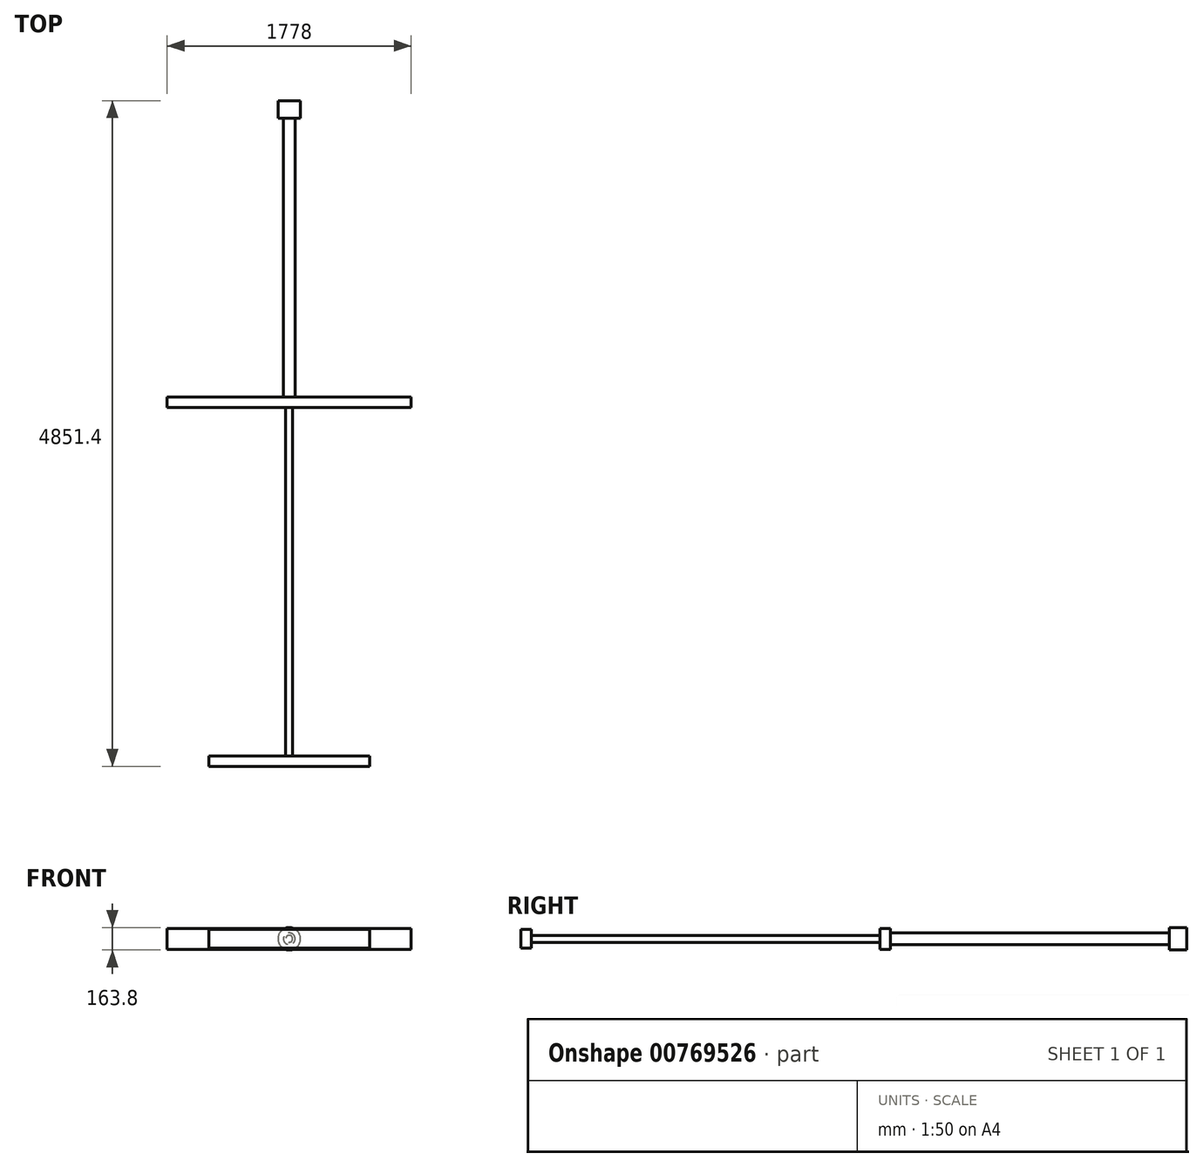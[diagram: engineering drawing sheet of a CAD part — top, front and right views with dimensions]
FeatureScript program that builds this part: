
annotation { "Feature Type Name" : "Feature", "Feature Type Description" : "" }
export const myFeature = defineFeature(function(context is Context, id is Id, definition is map)
    precondition{}
    {
        {
            var Q0;
            Q0=qCreatedBy(makeId("Front.planeOp"),FACE);
            var sketch = newSketch(context, id + "F0", { "sketchPlane" : qUnion([Q0])});
            skCircle(sketch, "E0", {"center": v(0, 0) * mm, "radius": 25.4 * mm});
            skSolve(sketch);
        }
        {
            var Q0;
            Q0 = qSketchRegion(id + "F0", true);
            extrude(context, id + "F1", {"entities" : qUnion([Q0]), "depth" : 2540 * mm, "offsetDistance" : 25.4 * mm});
        }
        {
            var Q0;
            Q0=makeQuery(id+"F1.opExtrude","CAP_FACE",FACE,{"disambiguationData":[OSD([sQuery(id+"F0.wireOp",EDGE,"E0")])],"isStart":false});
            var sketch = newSketch(context, id + "F2", { "sketchPlane" : qUnion([Q0])});
            skLineSegment(sketch, "E1.bottom", {"start": v(-585.14, 67.26) * mm, "end": v(585.14, 67.26) * mm});
            skLineSegment(sketch, "E1.top", {"start": v(-585.14, -67.26) * mm, "end": v(585.14, -67.26) * mm});
            skLineSegment(sketch, "E1.left", {"start": v(-585.14, 67.26) * mm, "end": v(-585.14, -67.26) * mm});
            skLineSegment(sketch, "E1.right", {"start": v(585.14, 67.26) * mm, "end": v(585.14, -67.26) * mm});
            skPoint(sketch, "E1.middle", {"position": v(0, 0) * mm});
            skSolve(sketch);
        }
        {
            var Q0;
            Q0 = qSketchRegion(id + "F2", true);
            extrude(context, id + "F3", {"entities" : qUnion([Q0]), "operationType" : NewBodyOperationType.ADD, "depth" : 76.2 * mm, "offsetDistance" : 25.4 * mm});
        }
        {
            var Q0;
            Q0=makeQuery(id+"F1.opExtrude","CAP_FACE",FACE,{"disambiguationData":[OSD([sQuery(id+"F0.wireOp",EDGE,"E0")])],"isStart":true});
            var sketch = newSketch(context, id + "F4", { "sketchPlane" : qUnion([Q0])});
            skLineSegment(sketch, "E2.bottom", {"start": v(-889, 76.2) * mm, "end": v(889, 76.2) * mm});
            skLineSegment(sketch, "E2.top", {"start": v(-889, -76.2) * mm, "end": v(889, -76.2) * mm});
            skLineSegment(sketch, "E2.left", {"start": v(-889, 76.2) * mm, "end": v(-889, -76.2) * mm});
            skLineSegment(sketch, "E2.right", {"start": v(889, 76.2) * mm, "end": v(889, -76.2) * mm});
            skPoint(sketch, "E2.middle", {"position": v(0, 0) * mm});
            skSolve(sketch);
        }
        {
            var Q0;
            Q0 = qSketchRegion(id + "F4", true);
            extrude(context, id + "F5", {"entities" : qUnion([Q0]), "operationType" : NewBodyOperationType.ADD, "depth" : 76.2 * mm, "offsetDistance" : 25.4 * mm});
        }
        {
            var Q0;
            Q0=makeQuery(id+"F5.opExtrude","CAP_FACE",FACE,{"disambiguationData":[OSD([sQuery(id+"F4.wireOp",EDGE,"E2.bottom"),sQuery(id+"F4.wireOp",EDGE,"E2.top"),sQuery(id+"F4.wireOp",EDGE,"E2.left"),sQuery(id+"F4.wireOp",EDGE,"E2.right")])],"isStart":false});
            var sketch = newSketch(context, id + "F6", { "sketchPlane" : qUnion([Q0])});
            skCircle(sketch, "E3", {"center": v(0, 0) * mm, "radius": 42.38 * mm});
            skSolve(sketch);
        }
        {
            var Q0;
            Q0 = qSketchRegion(id + "F6", true);
            extrude(context, id + "F7", {"entities" : qUnion([Q0]), "operationType" : NewBodyOperationType.ADD, "depth" : 2032 * mm, "offsetDistance" : 25.4 * mm});
        }
        {
            var Q0;
            Q0=makeQuery(id+"F7.opExtrude","CAP_FACE",FACE,{"disambiguationData":[OSD([sQuery(id+"F6.wireOp",EDGE,"E3")])],"isStart":false});
            var sketch = newSketch(context, id + "F8", { "sketchPlane" : qUnion([Q0])});
            skCircle(sketch, "E4", {"center": v(0, 0) * mm, "radius": 81.9 * mm});
            skSolve(sketch);
        }
        {
            var Q0;
            Q0 = qSketchRegion(id + "F8", true);
            extrude(context, id + "F9", {"entities" : qUnion([Q0]), "operationType" : NewBodyOperationType.ADD, "depth" : 127 * mm, "offsetDistance" : 25.4 * mm});
        }
    });
